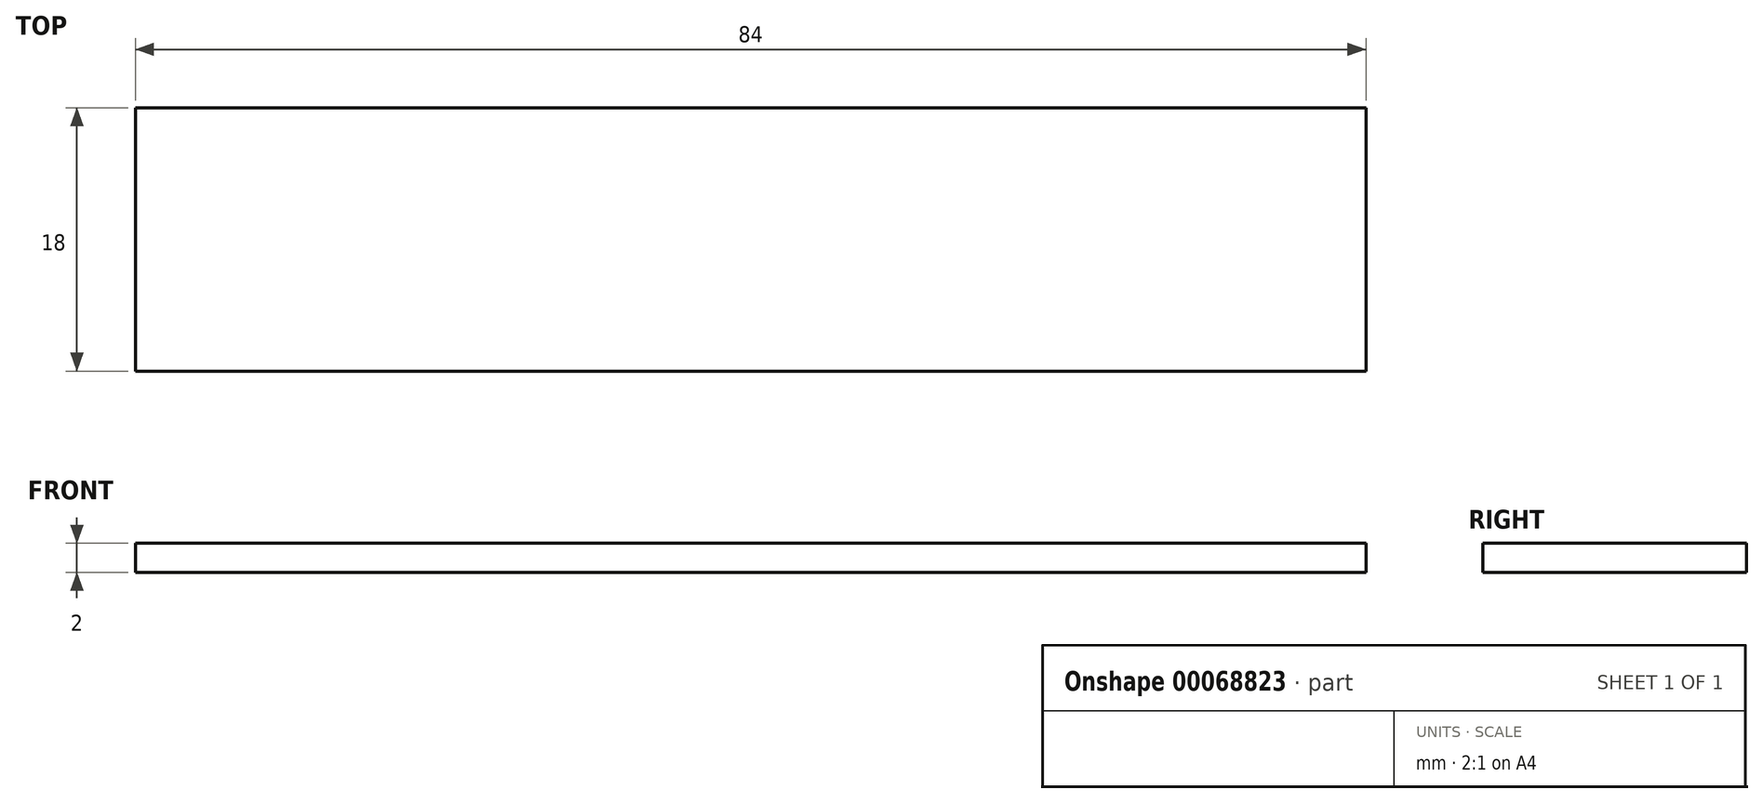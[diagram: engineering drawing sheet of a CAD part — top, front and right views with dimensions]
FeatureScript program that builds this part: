
annotation { "Feature Type Name" : "Feature", "Feature Type Description" : "" }
export const myFeature = defineFeature(function(context is Context, id is Id, definition is map)
    precondition{}
    {
        {
            var Q0;
            Q0=qCreatedBy(makeId("Top.planeOp"),FACE);
            var sketch = newSketch(context, id + "F0", { "sketchPlane" : qUnion([Q0])});
            skLineSegment(sketch, "E0.bottom", {"start": v(0, 0) * mm, "end": v(84, 0) * mm});
            skLineSegment(sketch, "E0.top", {"start": v(0, -18) * mm, "end": v(84, -18) * mm});
            skLineSegment(sketch, "E0.left", {"start": v(0, 0) * mm, "end": v(0, -18) * mm});
            skLineSegment(sketch, "E0.right", {"start": v(84, 0) * mm, "end": v(84, -18) * mm});
            skSolve(sketch);
        }
        {
            var Q0;
            Q0 = qSketchRegion(id + "F0", true);
            extrude(context, id + "F1", {"entities" : qUnion([Q0]), "depth" : 2 * mm});
        }
    });
